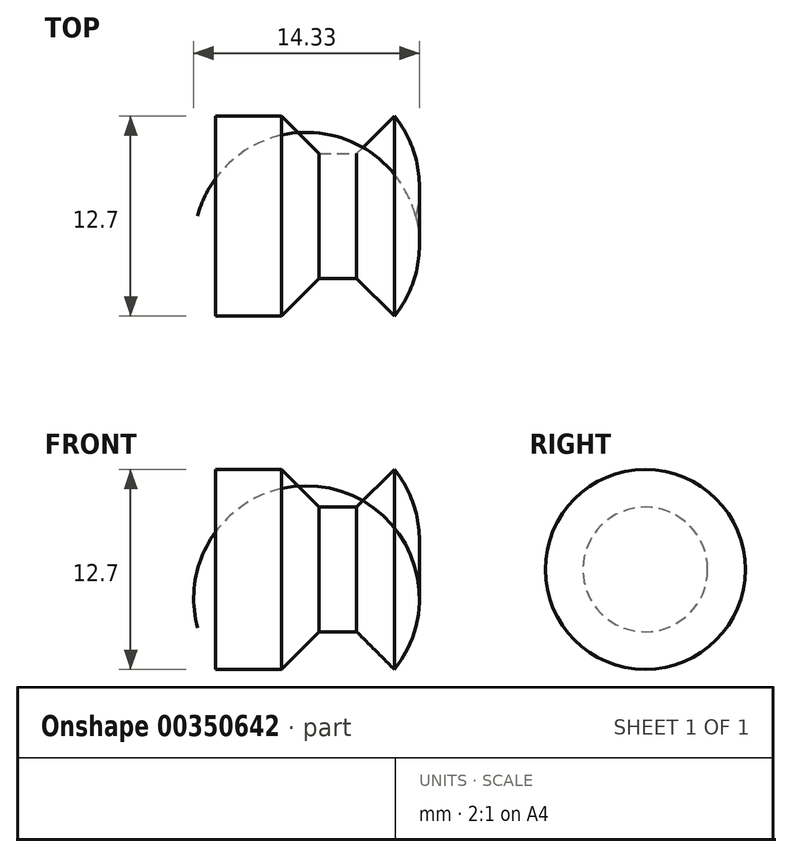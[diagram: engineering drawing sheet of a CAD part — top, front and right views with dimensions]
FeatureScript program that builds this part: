
annotation { "Feature Type Name" : "Feature", "Feature Type Description" : "" }
export const myFeature = defineFeature(function(context is Context, id is Id, definition is map)
    precondition{}
    {
        {
            var Q0;
            Q0=qCreatedBy(makeId("Front.planeOp"),FACE);
            var sketch = newSketch(context, id + "F0", { "sketchPlane" : qUnion([Q0])});
            skLineSegment(sketch, "E0", {"start": v(0, 0) * mm, "end": v(-12.7, 0) * mm});
            skLineSegment(sketch, "E1", {"start": v(-12.7, 0) * mm, "end": v(-12.7, 6.35) * mm});
            skLineSegment(sketch, "E2", {"start": v(-12.7, 6.35) * mm, "end": v(-8.52, 6.35) * mm});
            skLineSegment(sketch, "E3", {"start": v(-8.52, 6.35) * mm, "end": v(-6.13, 3.96) * mm});
            skLineSegment(sketch, "E4", {"start": v(-3.74, 3.96) * mm, "end": v(-1.34, 6.35) * mm});
            skArc(sketch, "E5", {"start": v(0, 0) * mm, "mid": v(0.09, 3.34) * mm, "end": v(-1.34, 6.35) * mm});
            skPoint(sketch, "E6.start.orphan", {"position": v(-3.74, 6.35) * mm});
            skLineSegment(sketch, "E7", {"start": v(-6.13, 3.96) * mm, "end": v(-3.74, 3.96) * mm});
            skSolve(sketch);
        }
        {
            var Q0;
            Q0=makeQuery(id+"F0.imprint","IMPRINT",FACE,{"disambiguationData":[TD([[makeQuery(id+"F0.imprint","IMPRINT",EDGE,{"derivedFrom":sQuery(id+"F0.wireOp",EDGE,"E0")}),-1.0]])]});
            var Q1;
            Q1=sQuery(id+"F0.wireOp",EDGE,"E0");
            revolve(context, id + "F1", {"entities" : qUnion([Q0]), "axis" : qUnion([Q1]), "revolveType" : RevolveType.FULL});
        }
    });
